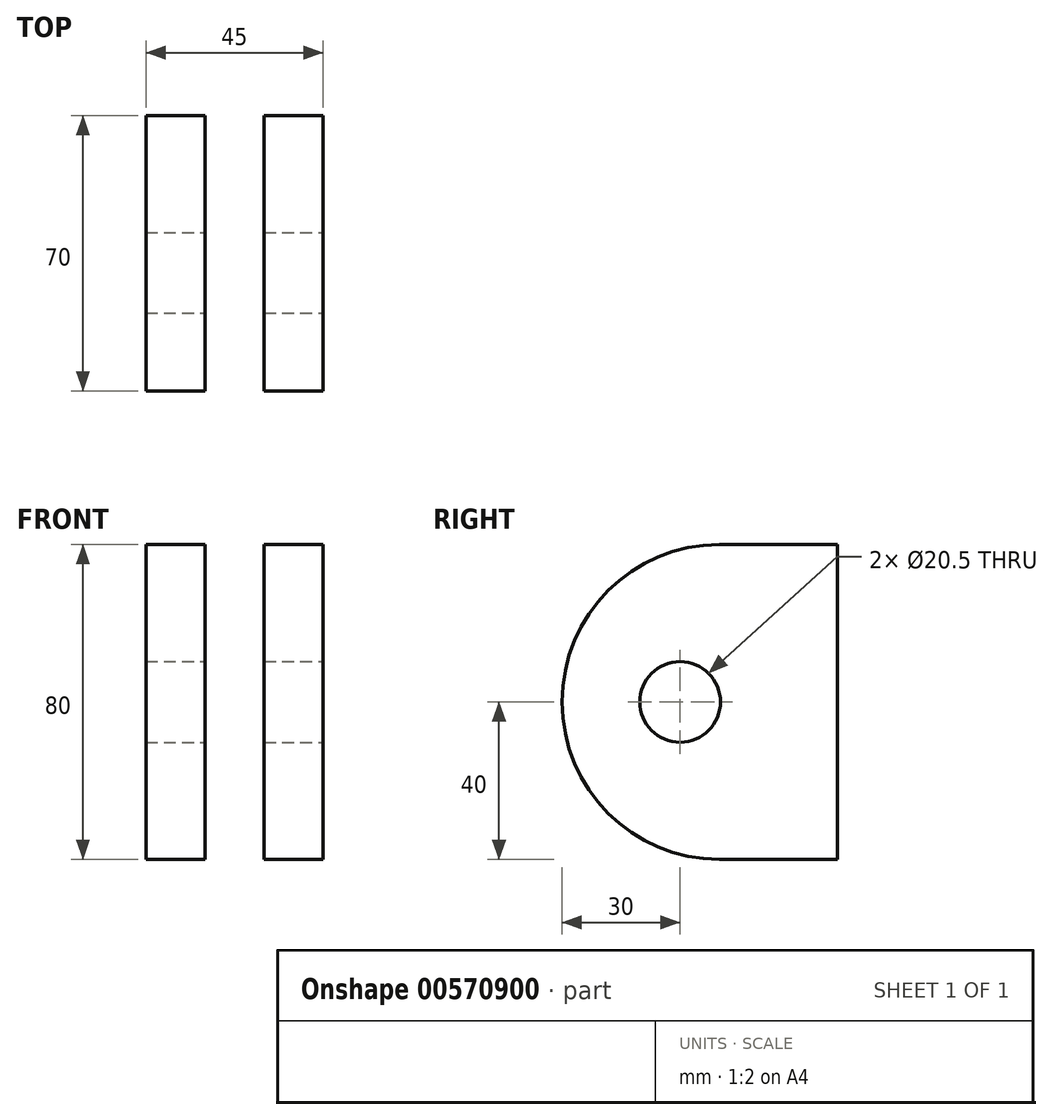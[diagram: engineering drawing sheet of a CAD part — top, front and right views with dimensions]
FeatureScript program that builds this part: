
annotation { "Feature Type Name" : "Feature", "Feature Type Description" : "" }
export const myFeature = defineFeature(function(context is Context, id is Id, definition is map)
    precondition{}
    {
        {
            var Q0;
            Q0=qCreatedBy(makeId("Front.planeOp"),FACE);
            var sketch = newSketch(context, id + "F0", { "sketchPlane" : qUnion([Q0])});
            skLineSegment(sketch, "E0.bottom", {"start": v(12.75, 76) * mm, "end": v(-2.25, 76) * mm});
            skLineSegment(sketch, "E0.top", {"start": v(12.75, -4) * mm, "end": v(-2.25, -4) * mm});
            skLineSegment(sketch, "E0.left", {"start": v(12.75, 76) * mm, "end": v(12.75, -4) * mm});
            skLineSegment(sketch, "E0.right", {"start": v(-2.25, 76) * mm, "end": v(-2.25, -4) * mm});
            skLineSegment(sketch, "E1.bottom", {"start": v(27.75, 76) * mm, "end": v(42.75, 76) * mm});
            skLineSegment(sketch, "E1.top", {"start": v(27.75, -4) * mm, "end": v(42.75, -4) * mm});
            skLineSegment(sketch, "E1.left", {"start": v(27.75, 76) * mm, "end": v(27.75, -4) * mm});
            skLineSegment(sketch, "E1.right", {"start": v(42.75, 76) * mm, "end": v(42.75, -4) * mm});
            skSolve(sketch);
        }
        {
            var Q0;
            Q0=makeQuery(id+"F0.imprint","IMPRINT",FACE,{"disambiguationData":[TD([[makeQuery(id+"F0.imprint","IMPRINT",EDGE,{"derivedFrom":sQuery(id+"F0.wireOp",EDGE,"E0.bottom")}),1.0]])]});
            var Q1;
            Q1=makeQuery(id+"F0.imprint","IMPRINT",FACE,{"disambiguationData":[TD([[makeQuery(id+"F0.imprint","IMPRINT",EDGE,{"derivedFrom":sQuery(id+"F0.wireOp",EDGE,"E1.bottom")}),-1.0]])]});
            extrude(context, id + "F1", {"entities" : qUnion([Q0, Q1]), "depth" : 70 * mm, "offsetDistance" : 25 * mm});
        }
        {
            var Q0;
            Q0=makeQuery(id+"F1.opExtrude","CAP_EDGE",EDGE,{"disambiguationData":[OSD([sQuery(id+"F0.wireOp",EDGE,"E0.bottom")])],"isStart":false});
            var Q1;
            Q1=makeQuery(id+"F1.opExtrude","CAP_EDGE",EDGE,{"disambiguationData":[OSD([sQuery(id+"F0.wireOp",EDGE,"E1.bottom")])],"isStart":false});
            var Q2;
            Q2=makeQuery(id+"F1.opExtrude","CAP_EDGE",EDGE,{"disambiguationData":[OSD([sQuery(id+"F0.wireOp",EDGE,"E1.top")])],"isStart":false});
            var Q3;
            Q3=makeQuery(id+"F1.opExtrude","CAP_EDGE",EDGE,{"disambiguationData":[OSD([sQuery(id+"F0.wireOp",EDGE,"E0.top")])],"isStart":false});
            fillet(context, id + "F2", {"entities" : qUnion([Q0, Q1, Q2, Q3]), "radius" : 40 * mm, "tangentPropagation" : true, "allowEdgeOverflow" : false});
        }
        {
            var Q0;
            Q0=makeQuery(id+"F1.opExtrude","SWEPT_FACE",FACE,{"disambiguationData":[OSD([sQuery(id+"F0.wireOp",EDGE,"E1.right")])]});
            var sketch = newSketch(context, id + "F3", { "sketchPlane" : qUnion([Q0])});
            skCircle(sketch, "E2", {"center": v(-40, 36) * mm, "radius": 10.25 * mm});
            skSolve(sketch);
        }
        {
            var Q0;
            Q0=makeQuery(id+"F3.imprint","IMPRINT",FACE,{"disambiguationData":[TD([[makeQuery(id+"F3.imprint","IMPRINT",EDGE,{"derivedFrom":sQuery(id+"F3.wireOp",EDGE,"E2")}),1.0]])]});
            var Q1;
            Q1=sQuery(id+"F3.wireOp",EDGE,"E2");
            extrude(context, id + "F4", {"entities" : qUnion([Q0]), "operationType" : NewBodyOperationType.REMOVE, "surfaceEntities" : qUnion([Q1]), "oppositeDirection" : true, "depth" : 86.5 * mm, "offsetDistance" : 25 * mm});
        }
        {
            var Q0;
            Q0=makeQuery(id+"F1.opExtrude","SWEPT_FACE",FACE,{"disambiguationData":[OSD([sQuery(id+"F0.wireOp",EDGE,"E0.right")])]});
            var sketch = newSketch(context, id + "F5", { "sketchPlane" : qUnion([Q0])});
            skCircle(sketch, "E3", {"center": v(40, 36) * mm, "radius": 10.25 * mm});
            skSolve(sketch);
        }
        {
            var Q0;
            Q0 = qSketchRegion(id + "F5", true);
            extrude(context, id + "F6", {"entities" : qUnion([Q0]), "operationType" : NewBodyOperationType.REMOVE, "oppositeDirection" : true, "depth" : 25 * mm, "offsetDistance" : 25 * mm});
        }
    });
